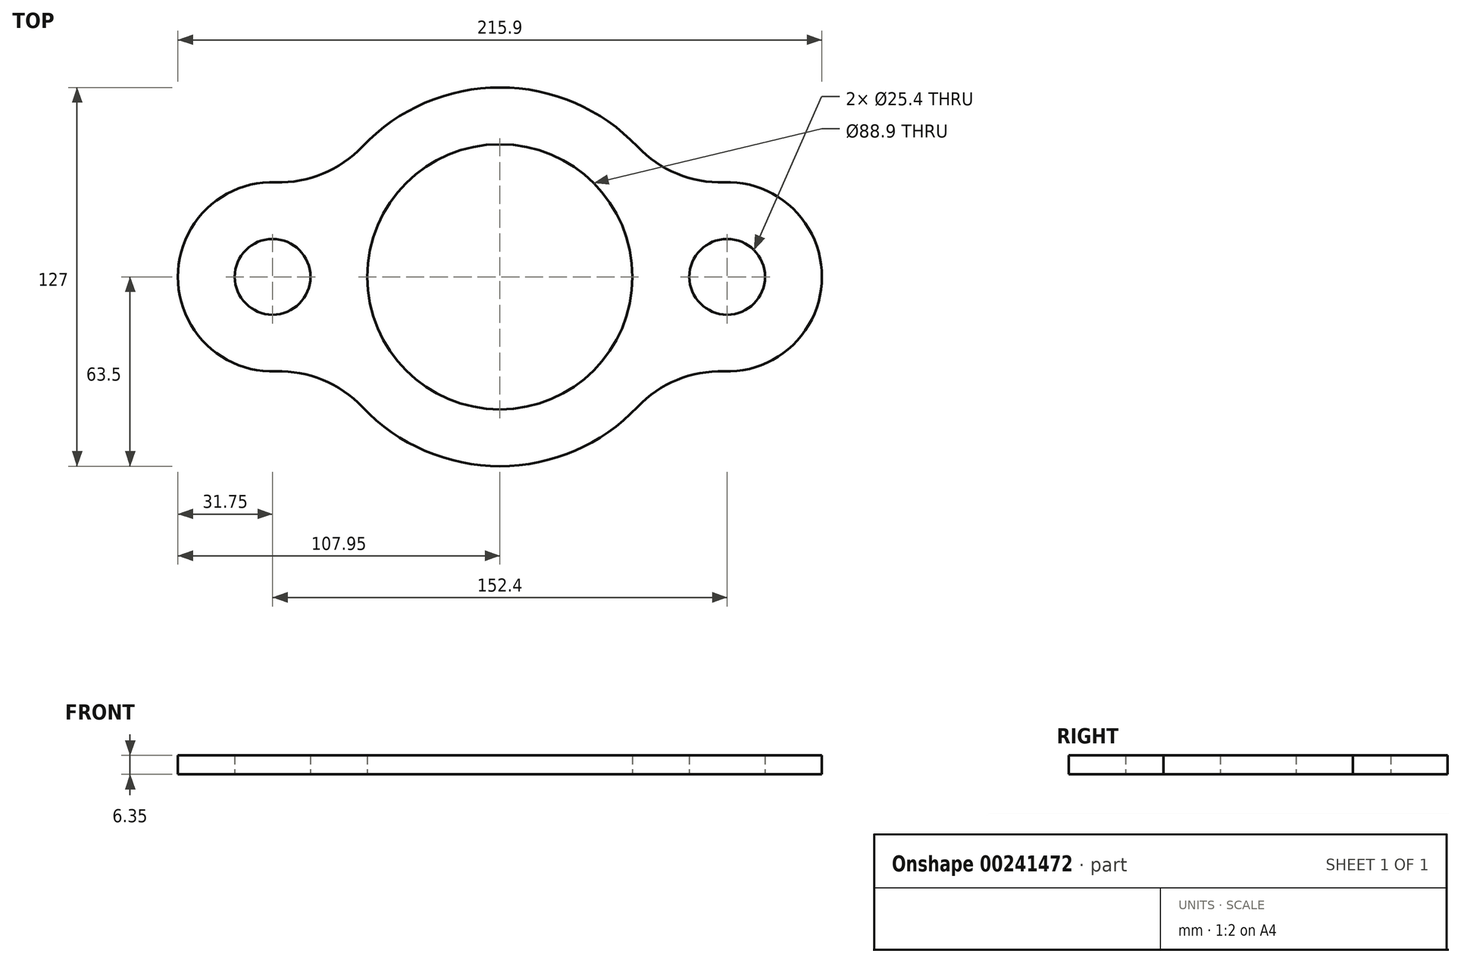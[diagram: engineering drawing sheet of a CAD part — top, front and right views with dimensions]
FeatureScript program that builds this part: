
annotation { "Feature Type Name" : "Feature", "Feature Type Description" : "" }
export const myFeature = defineFeature(function(context is Context, id is Id, definition is map)
    precondition{}
    {
        {
            var Q0;
            Q0=qCreatedBy(makeId("Top.planeOp"),FACE);
            var sketch = newSketch(context, id + "F0", { "sketchPlane" : qUnion([Q0])});
            skCircle(sketch, "E0", {"center": v(0, 0) * mm, "radius": 44.45 * mm});
            skCircle(sketch, "E1", {"center": v(76.2, 0) * mm, "radius": 12.7 * mm});
            skCircle(sketch, "E2", {"center": v(-76.2, 0) * mm, "radius": 12.7 * mm});
            skArc(sketch, "E3", {"start": v(-75.12, 31.73) * mm, "mid": v(-107.95, 0) * mm, "end": v(-75.12, -31.73) * mm});
            skArc(sketch, "E4", {"start": v(75.12, -31.73) * mm, "mid": v(107.95, 0) * mm, "end": v(75.12, 31.73) * mm});
            skArc(sketch, "E5", {"start": v(-46.14, -43.63) * mm, "mid": v(0, -63.5) * mm, "end": v(46.14, -43.63) * mm});
            skArc(sketch, "E6.trimOffspring", {"start": v(46.14, 43.63) * mm, "mid": v(0, 63.5) * mm, "end": v(-46.14, 43.63) * mm});
            skPoint(sketch, "E7.visualSharp", {"position": v(-57.94, 25.98) * mm});
            skArc(sketch, "E7.filletArc", {"start": v(-75.12, 31.73) * mm, "mid": v(-59.35, 34.56) * mm, "end": v(-46.14, 43.63) * mm});
            skPoint(sketch, "E8.visualSharp", {"position": v(-57.94, -25.98) * mm});
            skArc(sketch, "E8.filletArc", {"start": v(-46.14, -43.63) * mm, "mid": v(-59.35, -34.56) * mm, "end": v(-75.12, -31.73) * mm});
            skPoint(sketch, "E9.visualSharp", {"position": v(57.94, -25.98) * mm});
            skArc(sketch, "E9.filletArc", {"start": v(75.12, -31.73) * mm, "mid": v(59.35, -34.56) * mm, "end": v(46.14, -43.63) * mm});
            skPoint(sketch, "E10.visualSharp", {"position": v(57.94, 25.98) * mm});
            skArc(sketch, "E10.filletArc", {"start": v(46.14, 43.63) * mm, "mid": v(59.35, 34.56) * mm, "end": v(75.12, 31.73) * mm});
            skSolve(sketch);
        }
        {
            var Q0;
            Q0=makeQuery(id+"F0.imprint","IMPRINT",FACE,{"disambiguationData":[TD([[makeQuery(id+"F0.imprint","IMPRINT",EDGE,{"derivedFrom":sQuery(id+"F0.wireOp",EDGE,"E0")}),-1.0]])]});
            extrude(context, id + "F1", {"entities" : qUnion([Q0]), "depth" : 6.35 * mm});
        }
    });
